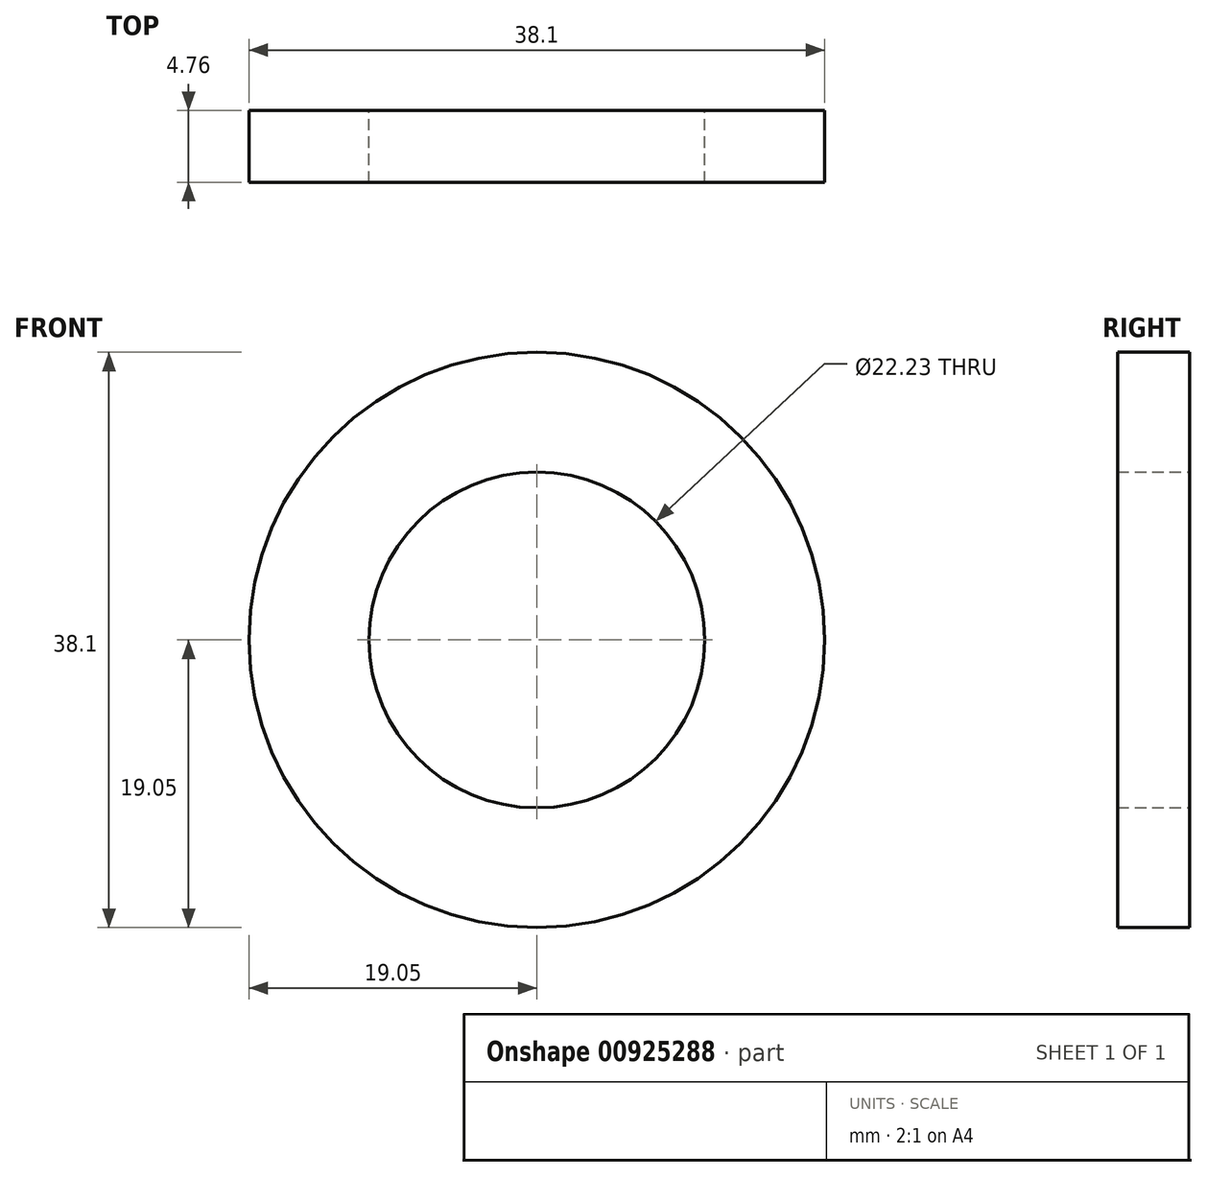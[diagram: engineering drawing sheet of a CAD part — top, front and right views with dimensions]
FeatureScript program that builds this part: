
annotation { "Feature Type Name" : "Feature", "Feature Type Description" : "" }
export const myFeature = defineFeature(function(context is Context, id is Id, definition is map)
    precondition{}
    {
        {
            var Q0;
            Q0=qCreatedBy(makeId("Front.planeOp"),FACE);
            var sketch = newSketch(context, id + "F0", { "sketchPlane" : qUnion([Q0])});
            skCircle(sketch, "E0", {"center": v(0, 0) * mm, "radius": 19.05 * mm});
            skCircle(sketch, "E1", {"center": v(0, 0) * mm, "radius": 11.11 * mm});
            skSolve(sketch);
        }
        {
            var Q0;
            Q0=makeQuery(id+"F0.imprint","IMPRINT",FACE,{"disambiguationData":[TD([[makeQuery(id+"F0.imprint","IMPRINT",EDGE,{"derivedFrom":sQuery(id+"F0.wireOp",EDGE,"E0")}),1.0]])]});
            extrude(context, id + "F1", {"entities" : qUnion([Q0]), "depth" : 4.76 * mm, "offsetDistance" : 25.4 * mm});
        }
    });
